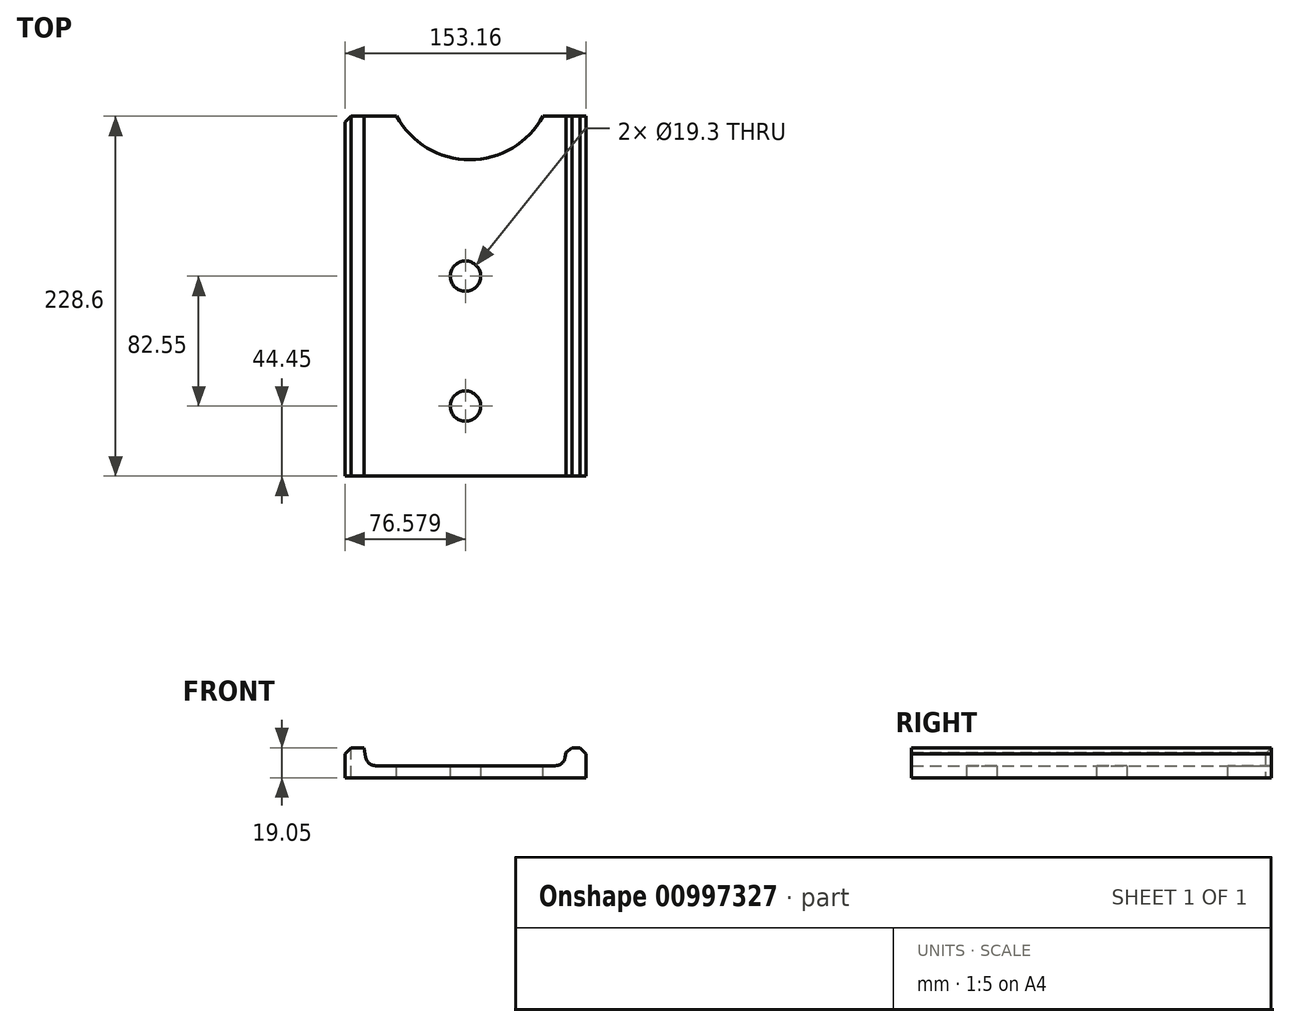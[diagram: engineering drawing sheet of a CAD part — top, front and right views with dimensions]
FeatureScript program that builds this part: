
annotation { "Feature Type Name" : "Feature", "Feature Type Description" : "" }
export const myFeature = defineFeature(function(context is Context, id is Id, definition is map)
    precondition{}
    {
        {
            var Q0;
            Q0=qCreatedBy(makeId("Front.planeOp"),FACE);
            var sketch = newSketch(context, id + "F0", { "sketchPlane" : qUnion([Q0])});
            skLineSegment(sketch, "E0.bottom", {"start": v(-168.04, 0) * mm, "end": v(-14.88, 0) * mm});
            skLineSegment(sketch, "E0.left", {"start": v(-168.04, 0) * mm, "end": v(-168.04, 19.05) * mm});
            skLineSegment(sketch, "E0.right", {"start": v(-14.88, 0) * mm, "end": v(-14.88, 19.05) * mm});
            skLineSegment(sketch, "E1", {"start": v(-155.87, 19.05) * mm, "end": v(-154.78, 12.87) * mm});
            skLineSegment(sketch, "E2", {"start": v(-148.53, 7.62) * mm, "end": v(-91.46, 7.62) * mm});
            skPoint(sketch, "E3.newPointA", {"position": v(-168.04, 7.62) * mm});
            skArc(sketch, "E3.filletArc", {"start": v(-154.78, 12.87) * mm, "mid": v(-152.6, 9.1) * mm, "end": v(-148.53, 7.62) * mm});
            skLineSegment(sketch, "E4.MirrorCS", {"start": v(-27.05, 19.05) * mm, "end": v(-28.14, 12.87) * mm});
            skPoint(sketch, "E5.MirrorP", {"position": v(-14.88, -32) * mm});
            skLineSegment(sketch, "E6.MirrorCS", {"start": v(-34.4, 7.62) * mm, "end": v(-91.46, 7.62) * mm});
            skArc(sketch, "E7.MirrorCS", {"start": v(-28.14, 12.87) * mm, "mid": v(-30.31, 9.1) * mm, "end": v(-34.4, 7.62) * mm});
            skPoint(sketch, "E8.MirrorP", {"position": v(-14.88, 12.44) * mm});
            skPoint(sketch, "E9.MirrorP", {"position": v(-21.23, 12.44) * mm});
            skLineSegment(sketch, "E10", {"start": v(-168.04, 19.05) * mm, "end": v(-155.87, 19.05) * mm});
            skLineSegment(sketch, "E11", {"start": v(-27.05, 19.05) * mm, "end": v(-14.88, 19.05) * mm});
            skSolve(sketch);
        }
        {
            var Q0;
            Q0 = qSketchRegion(id + "F0", true);
            extrude(context, id + "F1", {"entities" : qUnion([Q0]), "depth" : 228.6 * mm, "offsetDistance" : 25.4 * mm});
        }
        {
            var Q0;
            Q0=makeQuery(id+"F1.opExtrude","SWEPT_EDGE",EDGE,{"disambiguationData":[OSD([sQuery(id+"F0.wireOp",EDGE,"E0.left"),sQuery(id+"F0.wireOp",EDGE,"E10")])]});
            var Q1;
            Q1=makeQuery(id+"F1.opExtrude","SWEPT_EDGE",EDGE,{"disambiguationData":[OSD([sQuery(id+"F0.wireOp",EDGE,"E0.right"),sQuery(id+"F0.wireOp",EDGE,"E11")])]});
            var Q2;
            Q2=makeQuery(id+"F1.opExtrude","CAP_EDGE",EDGE,{"disambiguationData":[OSD([sQuery(id+"F0.wireOp",EDGE,"E0.right")])],"isStart":true});
            var Q3;
            Q3=makeQuery(id+"F1.opExtrude","CAP_EDGE",EDGE,{"disambiguationData":[OSD([sQuery(id+"F0.wireOp",EDGE,"E0.left")])],"isStart":true});
            chamfer(context, id + "F2", {"entities" : qUnion([Q0, Q1, Q2, Q3]), "width" : 3.8 * mm, "tangentPropagation" : true});
        }
        {
            var Q0;
            Q0=makeQuery(id+"F1.opExtrude","SWEPT_FACE",FACE,{"disambiguationData":[OSD([sQuery(id+"F0.wireOp",EDGE,"E2"),sQuery(id+"F0.wireOp",EDGE,"E6.MirrorCS")])]});
            var sketch = newSketch(context, id + "F3", { "sketchPlane" : qUnion([Q0])});
            skCircle(sketch, "E12", {"center": v(-88.69, 25.4) * mm, "radius": 53.02 * mm});
            skSolve(sketch);
        }
        {
            var Q0;
            {var subQ0=sQuery(id+"F3.wireOp",EDGE,"E12");var subQ1=makeQuery(id+"F1.opExtrude","CAP_EDGE",EDGE,{"disambiguationData":[OSD([sQuery(id+"F0.wireOp",EDGE,"E2"),sQuery(id+"F0.wireOp",EDGE,"E6.MirrorCS")])],"isStart":false});var subQ2=makeQuery(id+"F3.imprint","INTERSECT",VERTEX,{"disambiguationData":[OD(0.0)],"derivedFrom":[subQ1,subQ0]});Q0=makeQuery(id+"F3.imprint","IMPRINT",FACE,{"disambiguationData":[TD([[makeQuery(id+"F3.imprint","IMPRINT",EDGE,{"disambiguationData":[TD([[subQ2,1.0]])],"derivedFrom":subQ0}),1.0]])]});}
            var Q1;
            {var subQ0=sQuery(id+"F3.wireOp",EDGE,"E12");var subQ1=makeQuery(id+"F1.opExtrude","CAP_EDGE",EDGE,{"disambiguationData":[OSD([sQuery(id+"F0.wireOp",EDGE,"E2"),sQuery(id+"F0.wireOp",EDGE,"E6.MirrorCS")])],"isStart":true});var subQ2=makeQuery(id+"F3.imprint","INTERSECT",VERTEX,{"disambiguationData":[OD(0.0)],"derivedFrom":[subQ1,subQ0]});Q1=makeQuery(id+"F3.imprint","IMPRINT",FACE,{"disambiguationData":[TD([[makeQuery(id+"F3.imprint","IMPRINT",EDGE,{"disambiguationData":[TD([[subQ2,-1.0]])],"derivedFrom":subQ0}),1.0]])]});}
            extrude(context, id + "F4", {"entities" : qUnion([Q0, Q1]), "operationType" : NewBodyOperationType.REMOVE, "oppositeDirection" : true, "depth" : 25.4 * mm, "offsetDistance" : 25.4 * mm});
        }
        {
            var Q0;
            Q0=makeQuery(id+"F1.opExtrude","SWEPT_FACE",FACE,{"disambiguationData":[OSD([sQuery(id+"F0.wireOp",EDGE,"E0.bottom")])]});
            var sketch = newSketch(context, id + "F5", { "sketchPlane" : qUnion([Q0])});
            skCircle(sketch, "E13", {"center": v(-91.46, 101.6) * mm, "radius": 9.65 * mm});
            skCircle(sketch, "E14", {"center": v(-91.46, 184.15) * mm, "radius": 9.65 * mm});
            skSolve(sketch);
        }
        {
            var Q0;
            Q0 = qSketchRegion(id + "F5", true);
            extrude(context, id + "F6", {"entities" : qUnion([Q0]), "operationType" : NewBodyOperationType.REMOVE, "oppositeDirection" : true, "depth" : 25.4 * mm, "offsetDistance" : 25.4 * mm});
        }
    });
